# Revit family: BOILER_RMAX_R600EVO_604-607
name_source: partatom
category: Generic Models
revit_build: Autodesk Revit 2014 (Build: 20130308_1515(x64)
units: mm (PartAtom-declared; Revit-internal decimal feet)

## types (4) — shared parameters
Assembly Code = D3020100
Condensate_ConnectionDia = 32 mm
Condensate_SpigotDia = 42 mm  [stored 0.137795 ft]
ControlPanel_Depth = 190 mm
ControlPanel_Height = 198 mm  [stored 0.649606 ft]
Density_Water_70 = 977.8000 kg/m³
Equipment_Fuel = Natural Gas (G20)
Equipment_Height = 1470 mm
Equipment_Power_Factor = 0.9
Equipment_Width = 746 mm  [stored 2.44751 ft]
Flue_GasTemp = 90 °C
Flue_SpigotDia = 304 mm  [stored 0.997375 ft]
Frequency = 50 Hz
HTGF_ConnectionDia = 65 mm
HTGF_SpigotDia = 76 mm
HTGR_ConnectionDia = 65 mm
HTGR_SpigotDia = 76 mm
Issue_Date = 07-09-2017
Issue_Rev = A
Manufacturer = Rendamax
Maximum_Overcurrent_Protection = 16 A
Panel_Width = 510 mm  [stored 1.67323 ft]
Phase = 3
Specific_Heat_Water = 4.2000 J/(g·°C)
UnitConvert_Area = 1 m²
Voltage = 400 V

## per-type parameters (varying)
| type | Air_ConnectionDia | Air_SpigotDia | Boiler_Nominal_Output_40_30 | Boiler_Nominal_Output_80_60 | Equipment_Apparent_Power | Equipment_Depth | Equipment_Fuel_Flow | Equipment_Rated_Power | Flue_ConnectionDia | Gas_ConnectionDia | Gas_SpigotDia | Model | Seasonal_Energy_Efficiency | UnitConvert_PressureFactor | Water_Content_HTG | Weight_Dry | Weight_Operating |
| R604 | 130 mm | 135 mm | 303 kW | 286 kW | 256 VA | 1152 mm | 26.7 m3/hr | 230 W | 200 mm | 40 mm | 48 mm | R600 EVO 604 | 98.2 | 1005854 | 60.0 L | 434.00 kg | 494.00 kg |
| R605 | 130 mm | 135 mm | 404 kW | 381 kW | 560 VA | 1302 mm | 35.6 m3/hr | 504 W | 250 mm | 40 mm | 48 mm | R600 EVO 605 | 98.3 | 1532772 | 63.0 L | 496.00 kg | 559.00 kg |
| R606 | 150 mm | 155 mm  [stored 0.50853 ft] | 505 kW | 477 kW | 689 VA | 1452 mm | 44.5 m3/hr | 620 W | 250 mm | 50 mm | 60 mm | R600 EVO 606 | 98.3 | 1041388 | 71.0 L | 540.00 kg | 611.00 kg |
| R607 | 150 mm | 155 mm  [stored 0.50853 ft] | 573 kW | 540 kW | 751 VA | 1602 mm  [stored 5.25591 ft] | 50.5 m3/hr | 676 W | 250 mm | 50 mm | 60 mm | R600 EVO 607 | 98.2 | 1350006 | 77.0 L | 595.00 kg | 672.00 kg |

note: column(s) folded — value = type name in every type: Type Comments

note: [stored X ft] marks values corroborated as IEEE doubles in the binary element streams (Revit-internal decimal feet)

## geometry (parser evidence)
native form markers: Sweep x9
no freeform markers — native parametric forms only
